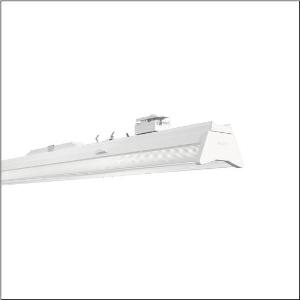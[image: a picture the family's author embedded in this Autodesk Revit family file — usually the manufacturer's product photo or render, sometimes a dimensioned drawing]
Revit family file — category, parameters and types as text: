
# Revit family: licross_r__21_performance_mo_52td16cn46xg_4d89
name_source: partatom
category: Lighting Fixtures
units: mm (PartAtom-declared; Revit-internal decimal feet)

## family parameters
Cut with Voids When Loaded = No
Host = Face
Light Source = No
Part Type = Normal
Room Calculation Point = No
Round Connector Dimension = Use Diameter
Shared = No

## types (1)
- --- (1 x LED, 6000 lm, 32 W, 4000K)
    Apparent Load = 32 VA
    CIE Flux Codes = 66 88 96 79 100
    Color Rendering = 80
    Color Temperature = 4000K
    Default Elevation = 1800 mm
    Description = Licross® 21 Performance MO, luminaire insert, of sheet steel, galvanised, coil coated, white, length: 1.500mm, width: 120mm, height: 123mm, LED rated luminous flux: 6.000lm, light colour: 840, SDCM (Standard Deviation of Colour Matching)MacAdam ≤ 3 SDCM (initial), control gear: ON/OFF Multilumen, CLOi, with plug, 3-pole, with phase selection, mains connection: 220..240V, AC, 50/60Hz, start of lifetime: 32W, end of service life: 38W, internal wiring halogen-free, primary light control with lens, of plastic, primary optical cover: cover, of PMMA, light emission: direct/indirect distribution, primary light characteristic: symmetric, protection rating (complete): IP54, insulation class (complete): insulation class I (protective earthing), certification: CE, ENEC, UKCA, protection symbol: D if used in an environment with non-conductive dust loads with corresponding accessories, impact resistance: IK06, permissible ambient temperature for indoor applications: -35..+55°C, corresponds to IFS (International Featured Standards) requirements for safety and quality in the food industry, reducing of maximum allowable ambient temperature of 5°C with ceiling mounting, LABS conformity tested according to VDMA 24364:2018-05, packaging unit: 1 piece
    Height = 114 mm
    Lamp = 1 x LED
    Lamp Light Flux = 6000 lm
    Lamp Power = 32 W
    Lamp count = 1
    Length = 1500 mm
    Luminous efficacy = 188 lm/W
    Manufacturer = Siteco
    ModVariant = No
    Model = 52TD16CN46XG
    Mounting Place = Ceiling
    Mounting Type = Pendant
    Number of Poles = 1
    OnlyDefault = Yes
    Power Factor = 1
    Product Name = Licross® 21 Performance MO
    Product group = luminaire insert | ceiling pendant
    ProductGroupID = 901
    Protection Class = Protection class I
    Protection Degree = IP 54
    RLX_Detail_Level = 1
    RLX_Emergency_Light_Flux = 0 lm
    RLX_Emergency_Type = 0
    RLX_Emergency_Type_DB = No
    RlxData = <blob elided: 31917 chars, md5=e0967c1a>
    Socket = socket
    Standby Power = 0 W
    System Light Flux = 6000 lm
    System Power = 32 W
    Type Comments = factory setting: luminous flux: 100 % | (A | C | E) | 74 mA
    Type Image = l_1256138.jpg
    URL = http://relux.com
    VarID = @adj_115455
    Voltage = 0 V
    Weight = 0.00 kg
    Width = 120 mm

## geometry (parser evidence)
native form markers: Blend x4, Sweep x11
no freeform markers — native parametric forms only
